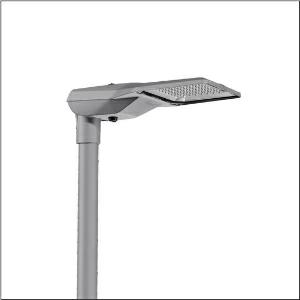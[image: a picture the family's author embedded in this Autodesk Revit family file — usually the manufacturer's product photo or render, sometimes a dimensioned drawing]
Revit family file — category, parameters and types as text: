
# Revit family: streetlight_sl_21_midi___st0_5a_5xe3b33t08mb_6d0d
name_source: partatom
category: Lighting Fixtures
units: mm (PartAtom-declared; Revit-internal decimal feet)

## family parameters
Cut with Voids When Loaded = No
Host = Face
Light Source = No
Part Type = Normal
Room Calculation Point = No
Round Connector Dimension = Use Diameter
Shared = No

## types (1)
- --- (1 x LED, 18270 lm, 136 W, 3000K)
    Apparent Load = 136 VA
    CIE Flux Codes = 41 75 97 100 100
    Color Rendering = 70
    Color Temperature = 3000K
    Default Elevation = 1800 mm
    Description = Streetlight SL 21 midi, mast luminaire, primary light control with lens, of PMMA, primary optical cover: cover, of toughened safety glass, transparent, light distribution: ST0.5a, light emission: direct distribution, primary light characteristic: asymmetric, installation type: side-entry, post-top, LED, High Power LED, rated luminous flux: 18.270lm, luminous efficacy: 134lm/W, light colour: 730, colour temperature: 3000K, control: overheat protection, constant luminous flux control, time-dependent luminous flux control, flexible luminous flux parameterisation, presetting dimming logarithmic, mains connection: 230..240V, AC, 50/60Hz, start of lifetime: 136W, end of service life: 142W, reduction: 61W, luminaire housing, of diecast aluminium, powder-coated, Siteco® metallic grey (DB 702S), corrosivity category C5 mid according to DIN EN ISO 12944, please order mast flange separately, inclination adjustable: 0°, 5°, 10°, 15°, sealing non-destructively replaceable, multi-level sealing system, length: 644mm, width: 335mm, height: 110mm, mast flange for spigot size: 42mm (side-entry): 5XC10008XM4, 60/48mm (side-entry/post-top): 5XC10108XM2, 76/60mm (side-entry/post-top): 5XC10108XM1, Smart Interface below and above, protection rating (complete): IP66, insulation class (complete): insulation class II (safety insulation), certification: CE, ENEC, ENEC+, VDE, impact resistance: IK09, permissible operating ambient temperature for outdoor applications: -40..+50°C, standard-compliant lighting for roads and squares, packaging unit: 1 piece

Light Distribution: ST0.5a
    Height = 111 mm
    Lamp = 1 x LED
    Lamp Light Flux = 18270 lm
    Lamp Power = 136 W
    Lamp count = 1
    Length = 644 mm
    Luminous efficacy = 134 lm/W
    Manufacturer = Siteco
    ModVariant = No
    Model = 5XE3B33T08MB
    Number of Poles = 1
    OnlyDefault = Yes
    Power Factor = 1
    Product Name = Streetlight SL 21 midi | ST0.5a
    Product group = mast luminaire | pylon top
    ProductGroupID = 6100
    Protection Class = Protection class II
    Protection Degree = IP 66
    RLX_Detail_Level = 1
    RLX_Emergency_Light_Flux = 0 lm
    RLX_Emergency_Type = 0
    RLX_Emergency_Type_DB = No
    RlxData = <blob elided: 102333 chars, md5=962790fc>
    Socket = socket
    Standby Power = 0 W
    System Light Flux = 18270 lm
    System Power = 136 W
    Type Comments = factory setting: luminous flux: 100 % | dim-lin: 254 | 695 mA
    Type Image = l_1004304.jpg
    URL = http://relux.com
    VarID = @adj_144121
    Voltage = 0 V
    Weight = 0.00 kg
    Width = 336 mm

## geometry (parser evidence)
native form markers: Blend x4, Sweep x9
no freeform markers — native parametric forms only
